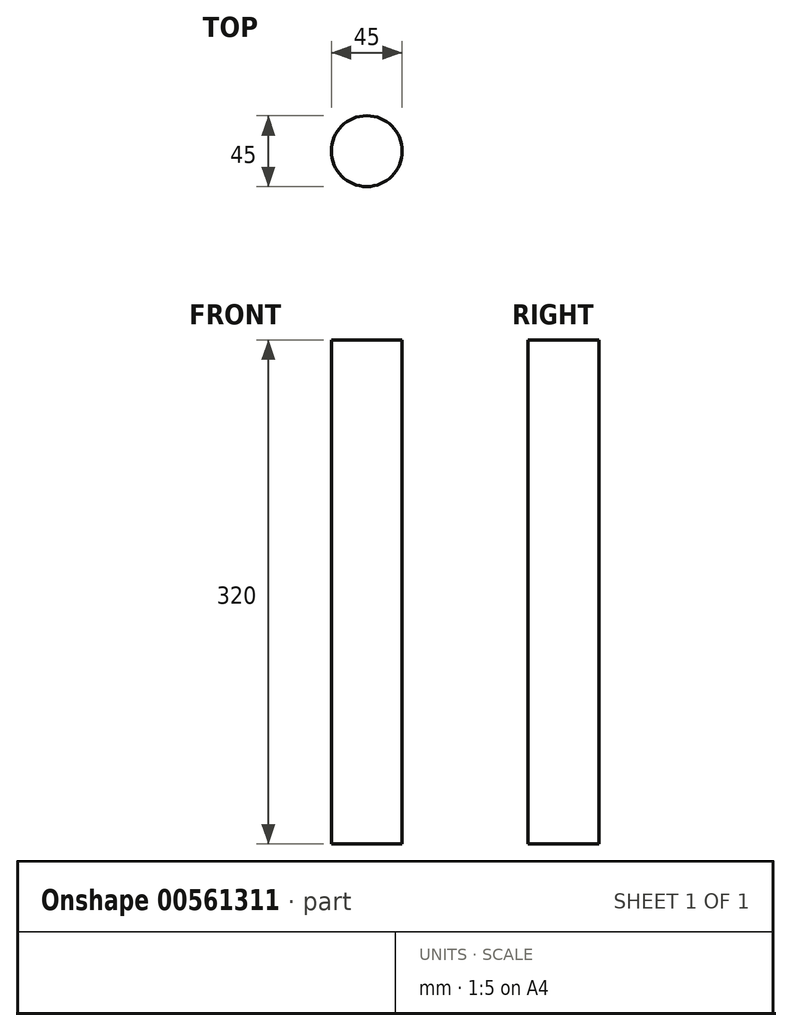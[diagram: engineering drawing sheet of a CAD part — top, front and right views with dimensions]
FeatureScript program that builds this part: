
annotation { "Feature Type Name" : "Feature", "Feature Type Description" : "" }
export const myFeature = defineFeature(function(context is Context, id is Id, definition is map)
    precondition{}
    {
        {
            var Q0;
            Q0=qCreatedBy(makeId("Top.planeOp"),FACE);
            var sketch = newSketch(context, id + "F0", { "sketchPlane" : qUnion([Q0])});
            skCircle(sketch, "E0", {"center": v(0, 0) * mm, "radius": 22.5 * mm});
            skSolve(sketch);
        }
        {
            var Q0;
            Q0=makeQuery(id+"F0.imprint","IMPRINT",FACE,{"disambiguationData":[TD([[makeQuery(id+"F0.imprint","IMPRINT",EDGE,{"derivedFrom":sQuery(id+"F0.wireOp",EDGE,"E0")}),1.0]])]});
            extrude(context, id + "F1", {"entities" : qUnion([Q0]), "depth" : 320 * mm, "offsetDistance" : 25 * mm});
        }
    });
